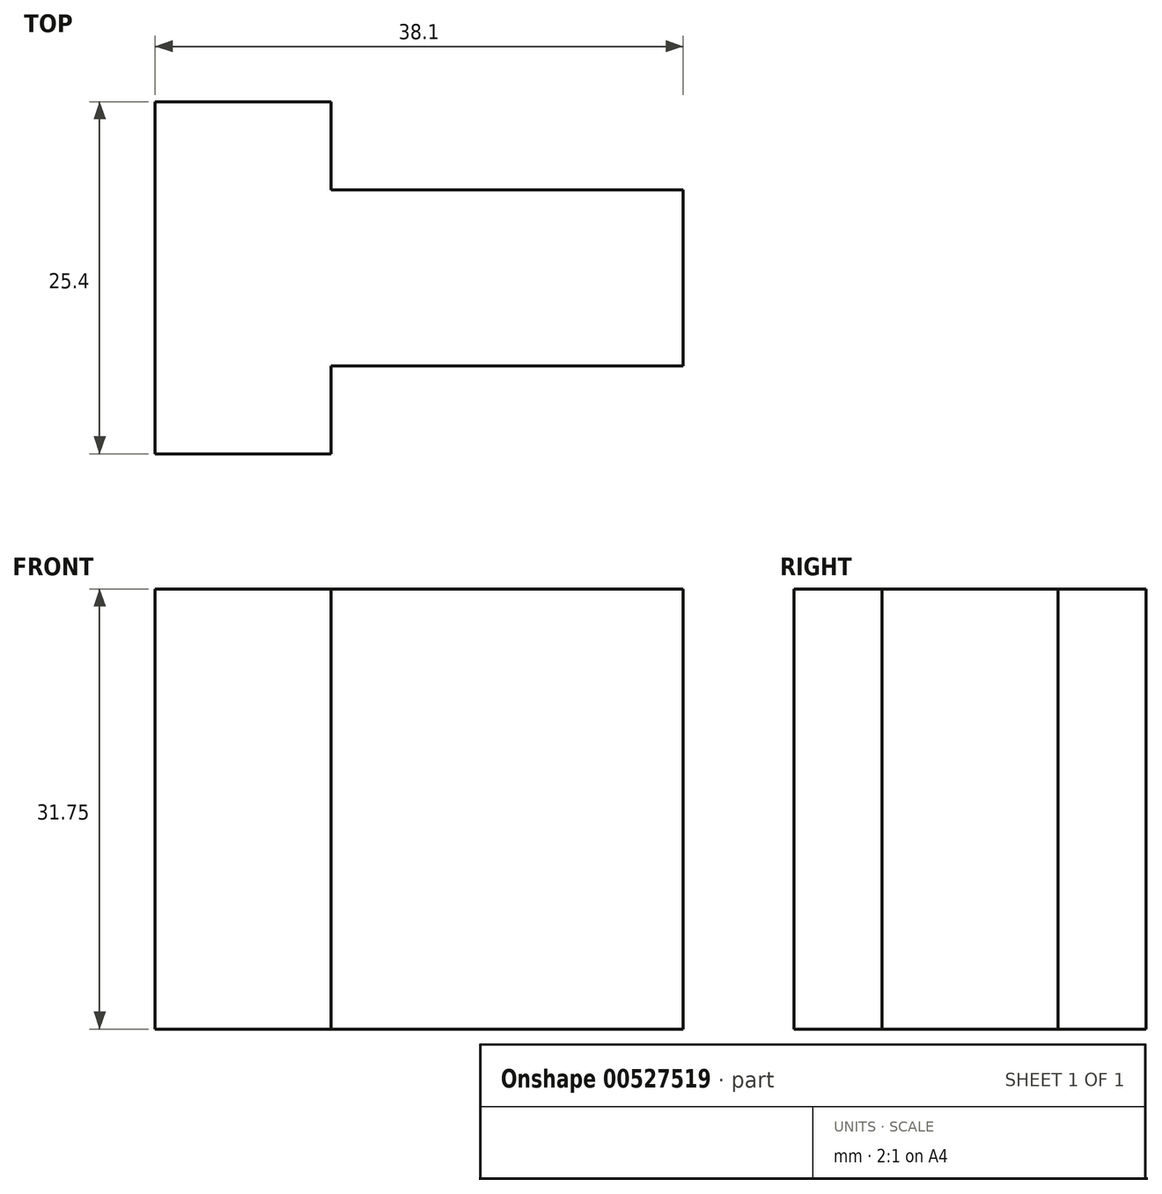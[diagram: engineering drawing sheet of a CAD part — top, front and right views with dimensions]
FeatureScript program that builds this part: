
annotation { "Feature Type Name" : "Feature", "Feature Type Description" : "" }
export const myFeature = defineFeature(function(context is Context, id is Id, definition is map)
    precondition{}
    {
        {
            var Q0;
            Q0=qCreatedBy(makeId("Top.planeOp"),FACE);
            var sketch = newSketch(context, id + "F0", { "sketchPlane" : qUnion([Q0])});
            skLineSegment(sketch, "E0", {"start": v(0, 0) * mm, "end": v(12.7, 0) * mm});
            skLineSegment(sketch, "E1", {"start": v(12.7, 6.35) * mm, "end": v(12.7, 0) * mm});
            skLineSegment(sketch, "E2", {"start": v(12.7, 6.35) * mm, "end": v(38.1, 6.35) * mm});
            skLineSegment(sketch, "E3", {"start": v(38.1, 6.35) * mm, "end": v(38.1, 19.05) * mm});
            skLineSegment(sketch, "E4", {"start": v(38.1, 19.05) * mm, "end": v(12.7, 19.05) * mm});
            skLineSegment(sketch, "E5", {"start": v(12.7, 19.05) * mm, "end": v(12.7, 25.4) * mm});
            skLineSegment(sketch, "E6", {"start": v(12.7, 25.4) * mm, "end": v(0, 25.4) * mm});
            skLineSegment(sketch, "E7", {"start": v(0, 25.4) * mm, "end": v(0, 0) * mm});
            skSolve(sketch);
        }
        {
            var Q0;
            Q0=makeQuery(id+"F0.imprint","IMPRINT",FACE,{"disambiguationData":[TD([[makeQuery(id+"F0.imprint","IMPRINT",EDGE,{"derivedFrom":sQuery(id+"F0.wireOp",EDGE,"E0")}),1.0]])]});
            extrude(context, id + "F1", {"entities" : qUnion([Q0]), "depth" : 31.75 * mm, "offsetDistance" : 25.4 * mm});
        }
    });
